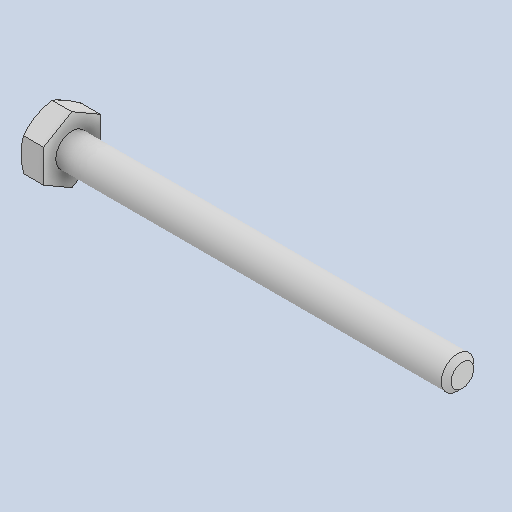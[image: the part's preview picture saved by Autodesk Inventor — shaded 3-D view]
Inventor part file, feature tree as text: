
AUTODESK INVENTOR PART (.ipt)
format: ipt  version: 2023 (Build 270158030, 158C)  size: 127,488 bytes
history: native  units: in
note: dims shown in document units (in); Inventor stores cm internally (conversion verified against a paired STEP export)
features: chamfer x1
ambient origin geometry x8: Origin, YZ Plane, XZ Plane, XY Plane, X Axis, Y Axis, Z Axis, Center Point
bodies: Solid1 (feature_tree)
feature tree (1):
  chamfer  "Chamfer1"  [1 undecoded]
note: 1 required parameter value undecoded (feature->parameter linkage not recoverable at this tier; creation-order binding heuristic only, values carry confidence <= 0.55)
